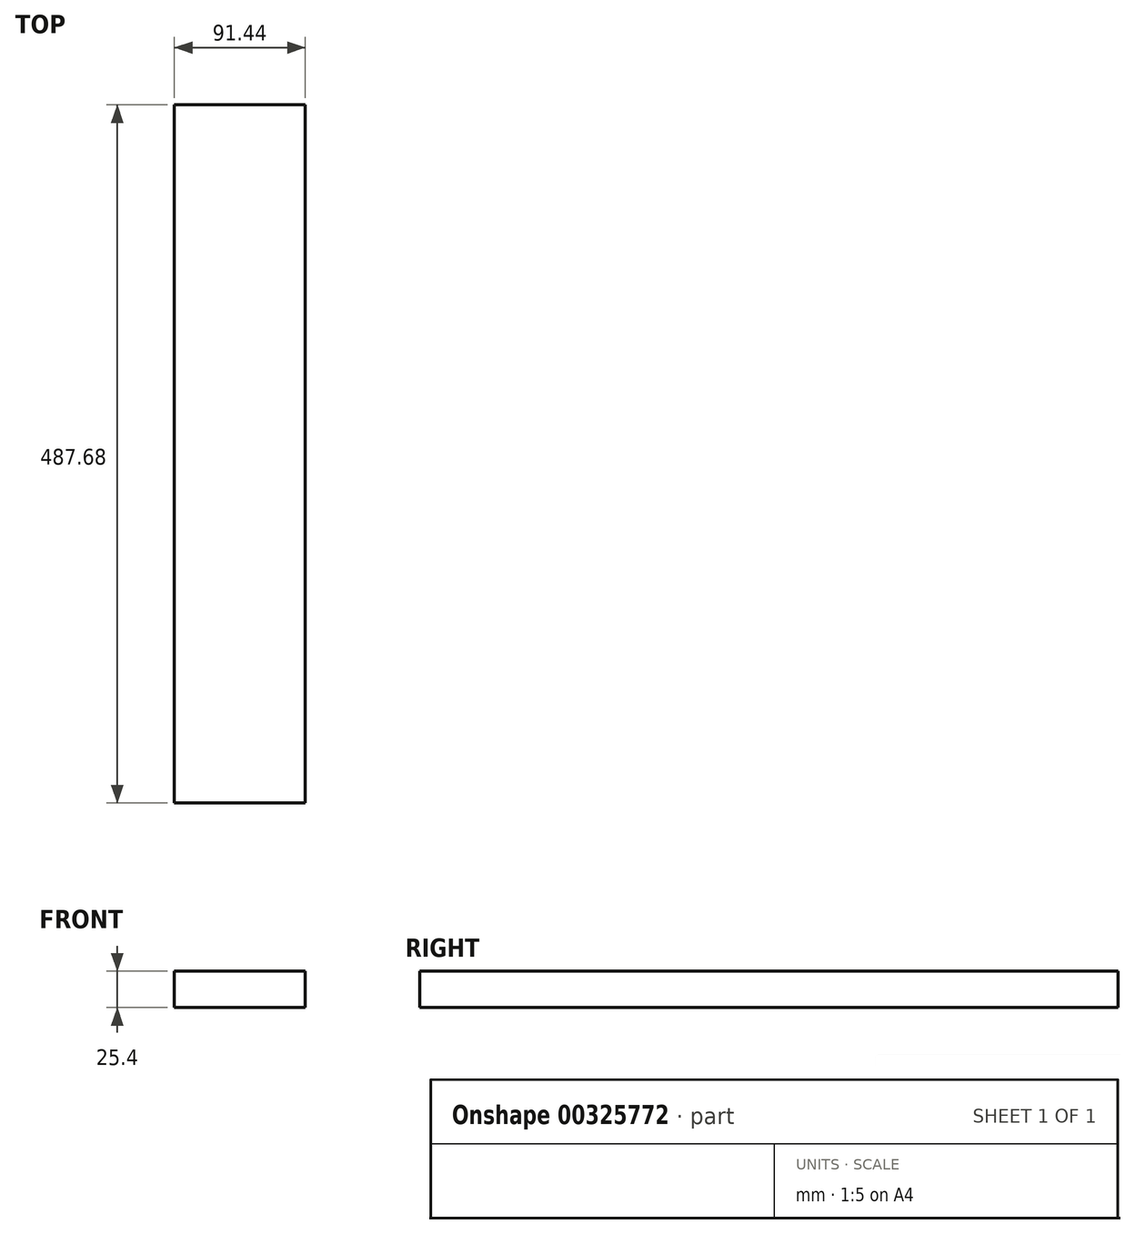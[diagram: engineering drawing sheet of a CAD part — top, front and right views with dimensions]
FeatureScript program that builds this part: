
annotation { "Feature Type Name" : "Feature", "Feature Type Description" : "" }
export const myFeature = defineFeature(function(context is Context, id is Id, definition is map)
    precondition{}
    {
        {
            var Q0;
            Q0=qCreatedBy(makeId("Front.planeOp"),FACE);
            var sketch = newSketch(context, id + "F0", { "sketchPlane" : qUnion([Q0])});
            skLineSegment(sketch, "E0.bottom", {"start": v(-45.72, 25.4) * mm, "end": v(45.72, 25.4) * mm});
            skLineSegment(sketch, "E0.top", {"start": v(-45.72, 0) * mm, "end": v(45.72, 0) * mm});
            skLineSegment(sketch, "E0.left", {"start": v(-45.72, 25.4) * mm, "end": v(-45.72, 0) * mm});
            skLineSegment(sketch, "E0.right", {"start": v(45.72, 25.4) * mm, "end": v(45.72, 0) * mm});
            skSolve(sketch);
        }
        {
            var Q0;
            Q0 = qSketchRegion(id + "F0", true);
            extrude(context, id + "F1", {"entities" : qUnion([Q0]), "depth" : 487.68 * mm});
        }
    });
